# Revit family: SANINDUSA_110032004_Cetus_Cetuswallmountedtoilet370x535x370_V0
name_source: partatom
category: Plumbing Fixtures
revit_build: Autodesk Revit 2018 (Build: 20170223_1515(x64)
units: mm (PartAtom-declared; Revit-internal decimal feet)

## family parameters
Cut with Voids When Loaded = No
Host = Face
Part Type = Normal
Room Calculation Point = No
Round Connector Dimension = Use Diameter
Shared = No

## types (1)
- SANINDUSA_110032004_Cetus_Cetuswallmountedtoilet370x535x370_V0
    AssetType = Fixed
    CodePerformance = EN 997:2012  CL 1 - 6 A/C
    Color = white
    Constituents = Compatible toilet seats (not included):21031 - Cetus toilet seat with clipoff and slowclose system; 21011 - Cetus toilet seat with clipoff system; 21021 - Cetus toilet seat with clipoff; 21061 - Cetus toilet seat with clipoff and slowclose system; 41733xx ‐ SANGLASS WALL external frame w/ dual flushing cistern for wall hung WC; 4193311 – Pack SANSLIM built‐in frame w/ dual flushing cistern for wall hung WC + To‐Slim dual flush plate; 411023 ‐ SANDOUBLE free standing frame w/ dual flushing cistern for wall hung WC; 4103311 ‐ Moove dual flush plate; 40333 ‐ SANFIX frame w/ dual flushing cistern for wall hung WC (for brick walls); 40323 ‐ SANFIX free standing frame w/ dual flushing cistern for wall hung WC; 40233 ‐ SANFLUSH built‐in frame w/ dual flushing cistern for wall hung WC; 40633 ‐ SANSPACE frame w/ dual flushing cistern for wall hung WC; (for brick walls); 40533 ‐ SANBEST built‐in frame w/ dual flushing cistern for wall hung WC (for brick walls); 40003xx ‐ Orange dual flush plate; 40013xx ‐ Plan dual flush plate; 40023xx‐ Easy dual flush plate; 40033xx – Moon dual flush plate; 40043xx – Square dual flush plate;
    Default Elevation = 1219 mm
    Description = Soil appliance for the disposal of excrement.
    DrainSize = 100 mm  [stored 0.328084 ft]
    Element Type = TOILETPAN: Soil appliance for the disposal of excrement.
    Features = "Domestic and commercial use. Versatile timeless design. Seats with clipoff system easy to clean and slow close option. Back to wall WC."
    Finish = gloss
    InletDiameter = 0 mm  [stored 0 ft]
    Installation Instructions = https://www.tec.sanindusa.pt
    Manufacturer = Sanindusa
    ManufacturerName = Sanindusa
    ManufacturerURL = www.tec.sanindusa.pt
    Material = vitreous china
    Model = 110032004
    ModelNumber = 110032004
    ModelReference = Cetus
    Name = Cetus wall mounted toilet
    NominalHeight = 370 mm  [stored 1.21391 ft]
    NominalLength = 370 mm  [stored 1.21391 ft]
    NominalWidth = 535 mm  [stored 1.75525 ft]
    PanColor = white
    PanMaterial = vitreous china
    PanMounting = wallhung
    Pre-defined type (IFC) = TOILETPAN
    ProductInformation = https://www.tec.sanindusa.pt
    ProductionYear = 2002
    Size = 370x535x370
    ToiletPanType = washdown
    ToiletType = LooseCoupled
    Type (IFC) = IfcSanitaryTerminalType
    URL = www.tec.sanindusa.pt
    Version = 1
    WarrantyDescription = https://www.tec.sanindusa.pt
    WarrantyDurationParts = 5
    WarrantyDurationUnit = year
    Waste Connection = Yes
    Weight = 15.30 kg

note: [stored X ft] marks values corroborated as IEEE doubles in the binary element streams (Revit-internal decimal feet)

## geometry (parser evidence)
native form markers: Sweep x6
no freeform markers — native parametric forms only
